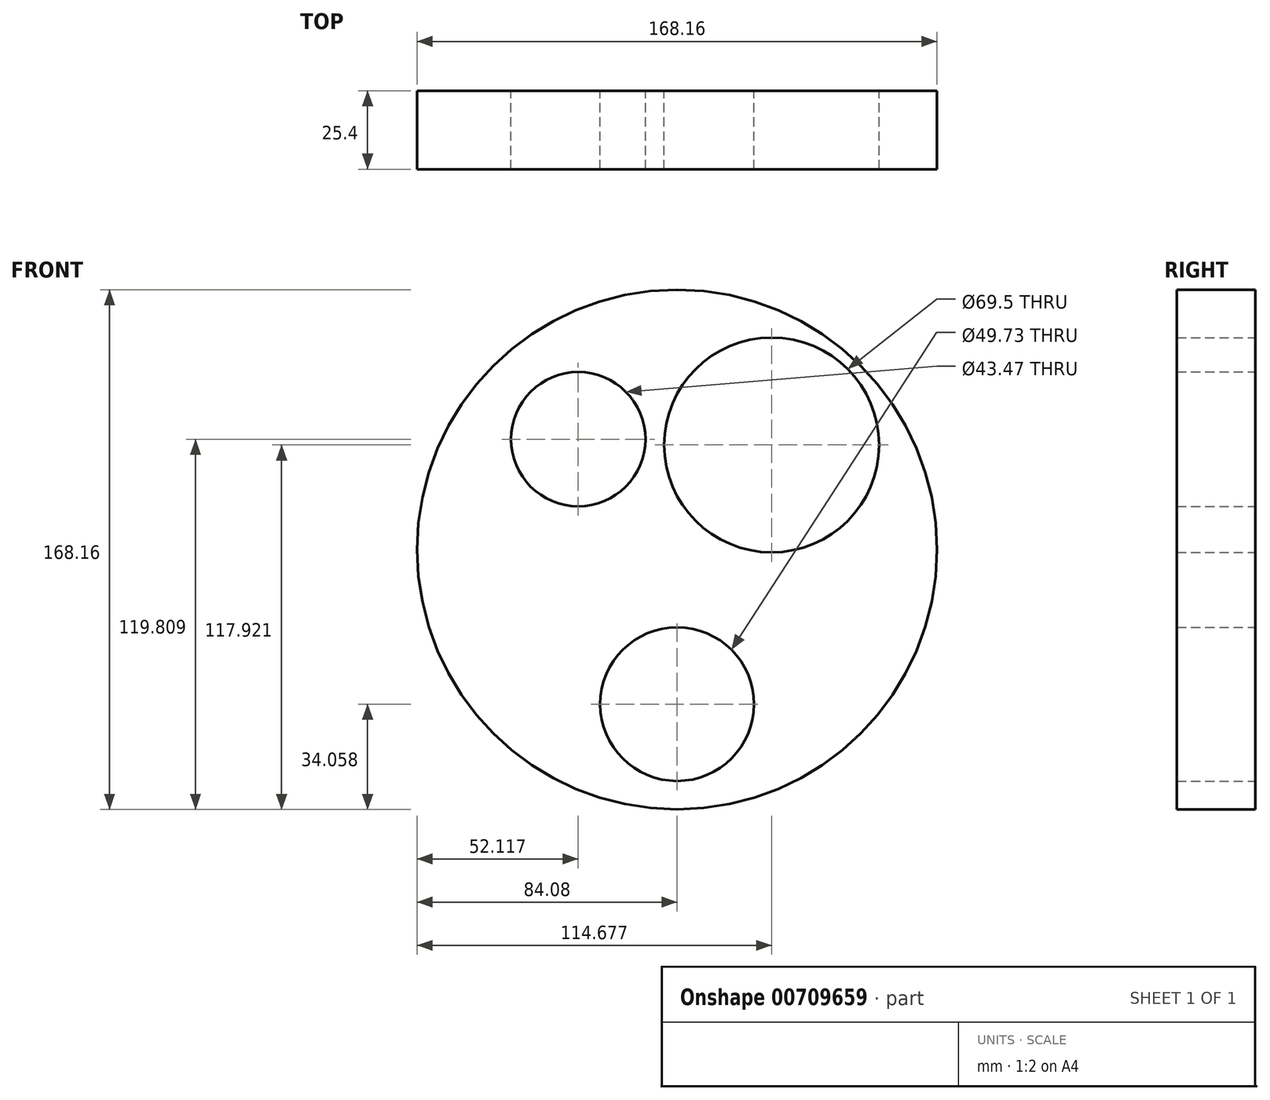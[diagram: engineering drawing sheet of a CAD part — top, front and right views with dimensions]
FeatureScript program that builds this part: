
annotation { "Feature Type Name" : "Feature", "Feature Type Description" : "" }
export const myFeature = defineFeature(function(context is Context, id is Id, definition is map)
    precondition{}
    {
        {
            var Q0;
            Q0=qCreatedBy(makeId("Front.planeOp"),FACE);
            var sketch = newSketch(context, id + "F0", { "sketchPlane" : qUnion([Q0])});
            skCircle(sketch, "E0", {"center": v(-31.96, 35.73) * mm, "radius": 21.74 * mm});
            skCircle(sketch, "E1", {"center": v(0, -50.02) * mm, "radius": 24.87 * mm});
            skCircle(sketch, "E2", {"center": v(30.6, 33.84) * mm, "radius": 34.75 * mm});
            skCircle(sketch, "E3", {"center": v(0, 0) * mm, "radius": 84.08 * mm});
            skSolve(sketch);
        }
        {
            var Q0;
            Q0=makeQuery(id+"F0.imprint","IMPRINT",FACE,{"disambiguationData":[TD([[makeQuery(id+"F0.imprint","IMPRINT",EDGE,{"derivedFrom":sQuery(id+"F0.wireOp",EDGE,"E0")}),-1.0]])]});
            extrude(context, id + "F1", {"entities" : qUnion([Q0]), "depth" : 25.4 * mm, "offsetDistance" : 25.4 * mm});
        }
    });
